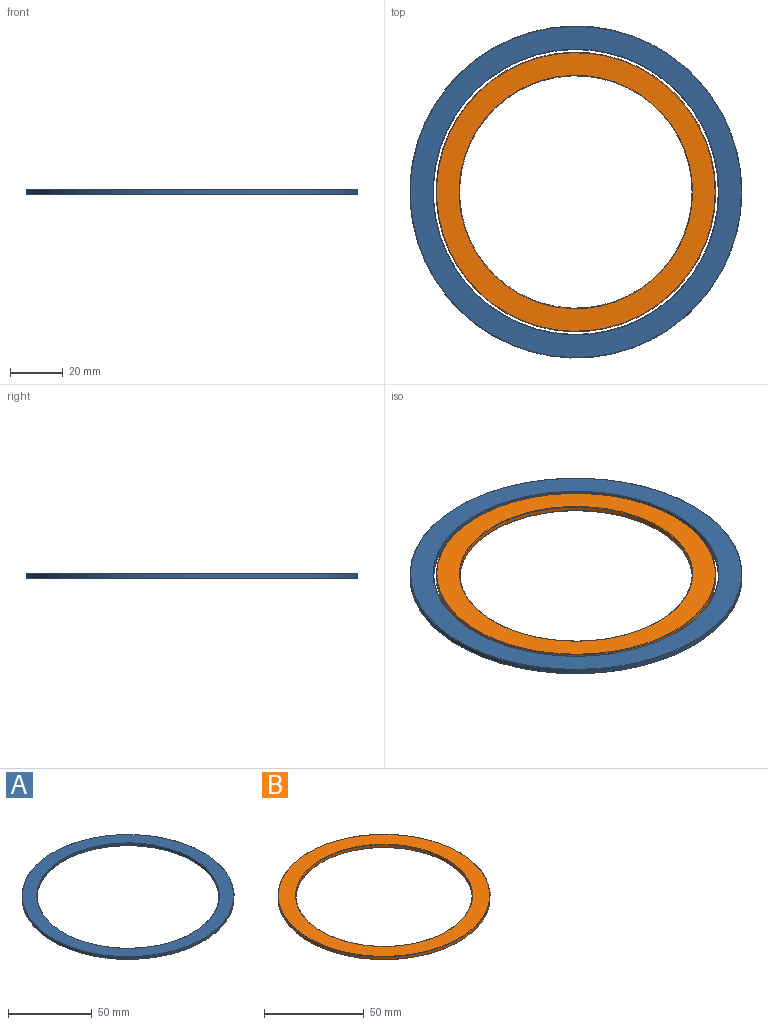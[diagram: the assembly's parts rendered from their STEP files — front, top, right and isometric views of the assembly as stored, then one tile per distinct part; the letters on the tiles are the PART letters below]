
ASSEMBLY  parts=2 mates=1
PART A: 8 faces, bbox 136.9x136.9x2 mm
  f0: cylinder r=54.25mm len=108.5mm, axis (0,0,-1), area 545.4mm2, adj f4,f6
  f1: cylinder r=63.25mm len=126.5mm, axis (0,0,-1), area 635.9mm2, adj f5,f7
  f2: plane 126.1x126.1mm, normal (0,0,1), area 3174.6mm2, adj f6,f7
  f3: plane 126.1x126.1mm, normal (0,0,-1), area 3174.6mm2, adj f4,f5
  f4: torus R=54.45mm, axis (0,0,1), area 107.2mm2, adj f0,f3
  f5: torus R=63.05mm, axis (0,0,1), area 124.7mm2, adj f1,f3
  f6: torus R=54.45mm, axis (0,0,1), area 107.2mm2, adj f0,f2
  f7: torus R=63.05mm, axis (0,0,1), area 124.7mm2, adj f1,f2
PART B: 8 faces, bbox 115.3x115.3x2 mm
  f0: cylinder r=44.25mm len=88.5mm, axis (0,0,-1), area 444.8mm2, adj f4,f6
  f1: cylinder r=53.25mm len=106.5mm, axis (0,0,-1), area 535.3mm2, adj f5,f7
  f2: plane 106.1x106.1mm, normal (0,0,1), area 2634.2mm2, adj f6,f7
  f3: plane 106.1x106.1mm, normal (0,0,-1), area 2634.2mm2, adj f4,f5
  f4: torus R=44.45mm, axis (0,0,1), area 87.5mm2, adj f0,f3
  f5: torus R=53.05mm, axis (0,0,1), area 105mm2, adj f1,f3
  f6: torus R=44.45mm, axis (0,0,1), area 87.5mm2, adj f0,f2
  f7: torus R=53.05mm, axis (0,0,1), area 105mm2, adj f1,f2
PLACE A t=(-15.45,-7.84,1.12)mm
PLACE B t=(-15.45,-7.84,1.12)mm
MATE revolute B.f0 <-> A.f0  axis (0,0,1) through (-15.45,-7.84,1.32)mm
